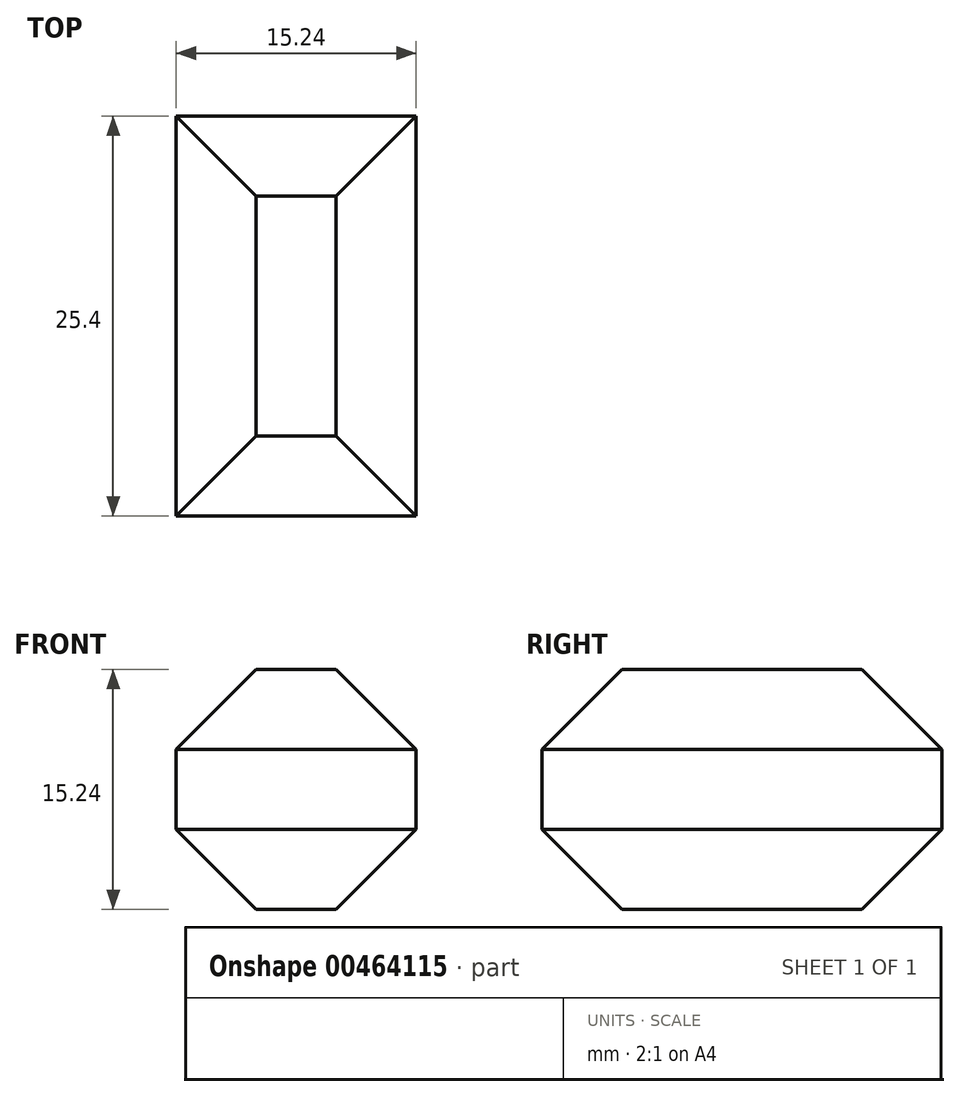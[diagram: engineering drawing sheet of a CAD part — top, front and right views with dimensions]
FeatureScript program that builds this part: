
annotation { "Feature Type Name" : "Feature", "Feature Type Description" : "" }
export const myFeature = defineFeature(function(context is Context, id is Id, definition is map)
    precondition{}
    {
        {
            var Q0;
            Q0=qCreatedBy(makeId("Front.planeOp"),FACE);
            var sketch = newSketch(context, id + "F0", { "sketchPlane" : qUnion([Q0])});
            skLineSegment(sketch, "E0.bottom", {"start": v(7.62, -7.62) * mm, "end": v(-7.62, -7.62) * mm});
            skLineSegment(sketch, "E0.top", {"start": v(7.62, 7.62) * mm, "end": v(-7.62, 7.62) * mm});
            skLineSegment(sketch, "E0.left", {"start": v(7.62, -7.62) * mm, "end": v(7.62, 7.62) * mm});
            skLineSegment(sketch, "E0.right", {"start": v(-7.62, -7.62) * mm, "end": v(-7.62, 7.62) * mm});
            skPoint(sketch, "E0.middle", {"position": v(0, 0) * mm});
            skLineSegment(sketch, "E1.bottom", {"start": v(15.24, -15.24) * mm, "end": v(-15.24, -15.24) * mm});
            skLineSegment(sketch, "E1.top", {"start": v(15.24, 15.24) * mm, "end": v(-15.24, 15.24) * mm});
            skLineSegment(sketch, "E1.left", {"start": v(15.24, -15.24) * mm, "end": v(15.24, 15.24) * mm});
            skLineSegment(sketch, "E1.right", {"start": v(-15.24, -15.24) * mm, "end": v(-15.24, 15.24) * mm});
            skSolve(sketch);
        }
        {
            var Q0;
            Q0=makeQuery(id+"F0.imprint","IMPRINT",FACE,{"disambiguationData":[TD([[makeQuery(id+"F0.imprint","IMPRINT",EDGE,{"derivedFrom":sQuery(id+"F0.wireOp",EDGE,"E0.bottom")}),-1.0]])]});
            extrude(context, id + "F1", {"entities" : qUnion([Q0]), "endBound" : BoundingType.SYMMETRIC, "depth" : 25.4 * mm});
        }
        {
            var Q0;
            Q0=makeQuery(id+"F1.opExtrude","CAP_EDGE",EDGE,{"disambiguationData":[OSD([sQuery(id+"F0.wireOp",EDGE,"E0.top")])],"isStart":false});
            var Q1;
            Q1=makeQuery(id+"F1.opExtrude","SWEPT_EDGE",EDGE,{"disambiguationData":[OSD([sQuery(id+"F0.wireOp",EDGE,"E0.top"),sQuery(id+"F0.wireOp",EDGE,"E0.left")])]});
            var Q2;
            Q2=makeQuery(id+"F1.opExtrude","CAP_EDGE",EDGE,{"disambiguationData":[OSD([sQuery(id+"F0.wireOp",EDGE,"E0.top")])],"isStart":true});
            var Q3;
            Q3=makeQuery(id+"F1.opExtrude","SWEPT_EDGE",EDGE,{"disambiguationData":[OSD([sQuery(id+"F0.wireOp",EDGE,"E0.top"),sQuery(id+"F0.wireOp",EDGE,"E0.right")])]});
            var Q4;
            Q4=makeQuery(id+"F1.opExtrude","CAP_EDGE",EDGE,{"disambiguationData":[OSD([sQuery(id+"F0.wireOp",EDGE,"E0.bottom")])],"isStart":false});
            var Q5;
            Q5=makeQuery(id+"F1.opExtrude","SWEPT_EDGE",EDGE,{"disambiguationData":[OSD([sQuery(id+"F0.wireOp",EDGE,"E0.bottom"),sQuery(id+"F0.wireOp",EDGE,"E0.right")])]});
            var Q6;
            Q6=makeQuery(id+"F1.opExtrude","SWEPT_EDGE",EDGE,{"disambiguationData":[OSD([sQuery(id+"F0.wireOp",EDGE,"E0.bottom"),sQuery(id+"F0.wireOp",EDGE,"E0.left")])]});
            var Q7;
            Q7=makeQuery(id+"F1.opExtrude","CAP_EDGE",EDGE,{"disambiguationData":[OSD([sQuery(id+"F0.wireOp",EDGE,"E0.bottom")])],"isStart":true});
            chamfer(context, id + "F2", {"entities" : qUnion([Q0, Q1, Q2, Q3, Q4, Q5, Q6, Q7]), "width" : 5.08 * mm, "tangentPropagation" : true});
        }
    });
